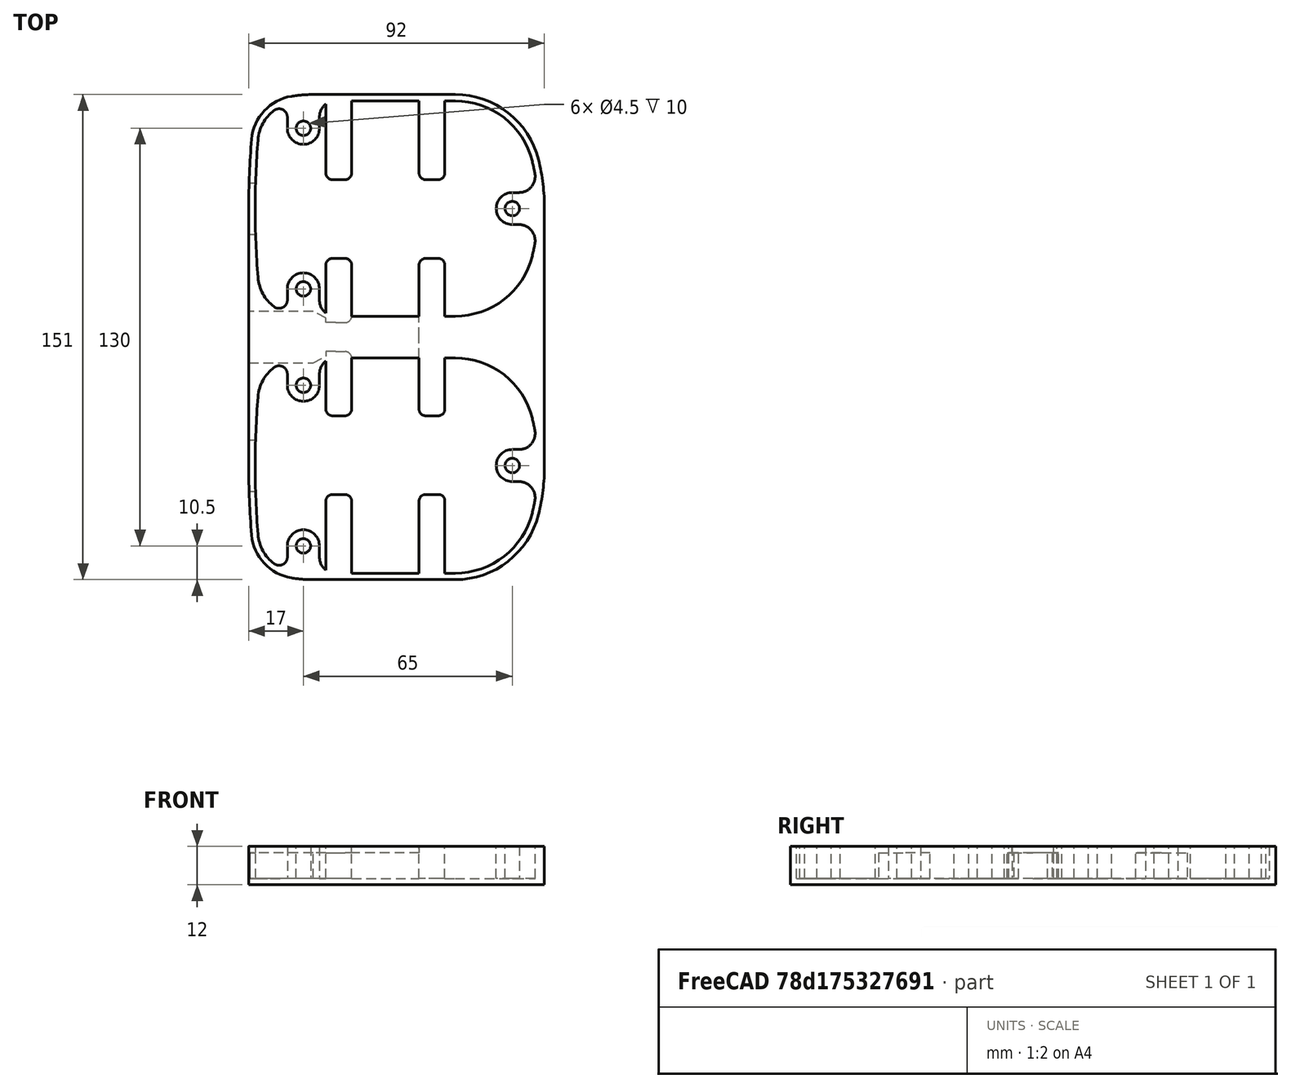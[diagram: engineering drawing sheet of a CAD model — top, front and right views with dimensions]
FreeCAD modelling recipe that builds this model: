
FCSTD DOCUMENT  (FreeCAD 0.21R33771 (Git))
Label: Makita LXT  - 18V - 2 x Bottom
License: Creative Commons Attribution 4.0
LicenseURL: https://creativecommons.org/licenses/by/4.0/
objects: Sketcher::SketchObject×6, PartDesign::Pocket×4, Mesh::Feature×3, PartDesign::Pad×2, Part::Feature×1, PartDesign::Body×1
note: 20 computed .brp shape members not serialized (recipe doc carries the construction recipe); baked Part::Feature solids carry a one-line shape summary decoded from their .brp

FEATURE [Mesh::Feature] XT60_top
  Placement = pos=(-27.47,40,-11) rot=(0,0,1;0rad)
FEATURE [Mesh::Feature] XT60_top001
  Placement = pos=(-27.47,-40,2) rot=(0,0,1;0rad)
FEATURE [Sketcher::SketchObject] Sketch
  FullyConstrained = true
  MapMode = 5
  Support = -> [XY_Plane]
  sketch-geometry (16):
    g0: ArcOfCircle CenterX=259.65 CenterY=40 CenterZ=0 NormalX=0 NormalY=0 NormalZ=1 AngleXU=0 Radius=259.65 StartAngle=3.05831 EndAngle=3.14159
    g1: ArcOfCircle CenterX=15.6319 CenterY=60.3702 CenterZ=0 NormalX=0 NormalY=0 NormalZ=1 AngleXU=0 Radius=14.7831 StartAngle=1.7292 EndAngle=3.05831
    g2: LineSegment StartX=20 StartY=75.5 StartZ=0 EndX=64.2 EndY=75.5 EndZ=0
    g3: ArcOfCircle CenterX=64.2 CenterY=48.7705 CenterZ=0 NormalX=0 NormalY=0 NormalZ=1 AngleXU=0 Radius=26.7295 StartAngle=0.24292 EndAngle=1.5708
    g4: ArcOfCircle CenterX=28.8084 CenterY=40 CenterZ=0 NormalX=0 NormalY=0 NormalZ=1 AngleXU=0 Radius=63.1916 StartAngle=0 EndAngle=0.24292
    g5: ArcOfCircle CenterX=20 CenterY=33.0247 CenterZ=0 NormalX=0 NormalY=0 NormalZ=1 AngleXU=0 Radius=42.4753 StartAngle=1.5708 EndAngle=1.7292
    g6: LineSegment StartX=0 StartY=40 StartZ=0 EndX=0 EndY=0 EndZ=0
    g7: LineSegment StartX=92 StartY=40 StartZ=0 EndX=92 EndY=0 EndZ=0
    g8: ArcOfCircle CenterX=259.65 CenterY=-40 CenterZ=0 NormalX=0 NormalY=0 NormalZ=1 AngleXU=0 Radius=259.65 StartAngle=3.14159 EndAngle=3.22488
    g9: ArcOfCircle CenterX=15.6319 CenterY=-60.3702 CenterZ=0 NormalX=0 NormalY=0 NormalZ=1 AngleXU=0 Radius=14.7831 StartAngle=3.22488 EndAngle=4.55399
    g10: LineSegment StartX=20 StartY=-75.5 StartZ=0 EndX=64.2 EndY=-75.5 EndZ=0
    g11: ArcOfCircle CenterX=64.2 CenterY=-48.7705 CenterZ=0 NormalX=0 NormalY=0 NormalZ=1 AngleXU=0 Radius=26.7295 StartAngle=4.71239 EndAngle=6.04026
    g12: ArcOfCircle CenterX=28.8084 CenterY=-40 CenterZ=0 NormalX=0 NormalY=0 NormalZ=1 AngleXU=0 Radius=63.1916 StartAngle=6.04026 EndAngle=6.28319
    g13: ArcOfCircle CenterX=20 CenterY=-33.0247 CenterZ=0 NormalX=0 NormalY=0 NormalZ=1 AngleXU=0 Radius=42.4753 StartAngle=4.55399 EndAngle=4.71239
    g14: LineSegment StartX=0 StartY=-40 StartZ=0 EndX=0 EndY=0 EndZ=0
    g15: LineSegment StartX=92 StartY=-40 StartZ=0 EndX=92 EndY=0 EndZ=0
  constraints (46):
    c: Horizontal(g2)
    c: DistanceX(g2) = 20
    c: DistanceY(g2) = 75.5
    c: DistanceX(g2,g2) = 44.2
    c: Tangent(g4,g3) = -1.5708
    c: Tangent(g3,g2) = 1.5708
    c: DistanceY(g3) = 55.2
    c: Tangent(g1,g0) = -1.5708
    c: Tangent(g5,g2) = 1.5708
    c: Tangent(g5,g1) = -1.5708
    c: DistanceX(g0) = 0.9
    c: DistanceX(g1) = 13.3
    c: DistanceY(g0) = 61.6
    c: Coincident(g6,g-1)
    c: Vertical(g6)
    c: PointOnObject(g7,g-1)
    c: Vertical(g7)
    c: Equal(g7,g6)
    c: DistanceY(g0) = 40
    c: DistanceX(g4) = 92
    c: Tangent(g7,g4) = 1.5708
    c: Tangent(g6,g0) = -1.5708
    c: Horizontal(g10)
    c: Tangent(g12,g11) = -1.5708
    c: Tangent(g11,g10) = -1.5708
    c: Tangent(g9,g8) = -1.5708
    c: Tangent(g13,g10) = -1.5708
    c: Tangent(g13,g9) = -1.5708
    c: Vertical(g14)
    c: Vertical(g15)
    c: Equal(g15,g14)
    c: Tangent(g15,g12) = -1.5708
    c: Tangent(g14,g8) = 1.5708
    c: Radius(g8) = 259.65  'Radius1'
    c: Radius(g9) = 14.7831  'Radius2'
    c: Radius(g13) = 42.4753  'Radius3'
    c: Radius(g11) = 26.7295  'Radius4'
    c: Radius(g12) = 63.1916  'Radius5'
    c: Coincident(g14,g6)
    c: Coincident(g15,g7)
    c: Equal(g12,g4)
    c: Equal(g11,g3)
    c: Equal(g5,g13)
    c: Equal(g9,g1)
    c: Symmetric(g8,g0,g-1)
    c: Symmetric(g1,g9,g-1)
FEATURE [PartDesign::Pad] Pad
  Direction = (0,0,1)
  Length = 12
  Length2 = 10
  Profile = -> Sketch
  ReferenceAxis = -> Sketch [N_Axis]
  Type = 0
FEATURE [Sketcher::SketchObject] Sketch001
  ExternalGeometry = -> [Sketch]
  FullyConstrained = false
  MapMode = 5
  Placement = pos=(0,0,12) rot=(0,0,1;0rad)
  Support = -> [Pad]
  expr: Constraints[4] = <<Sketch>>.Constraints.Radius1 - 2 mm
  expr: Constraints[5] = <<Sketch>>.Constraints.Radius4 - 2 mm
  expr: Constraints[6] = <<Sketch>>.Constraints.Radius5 - 2 mm
  sketch-geometry (68):
    g0: ArcOfCircle CenterX=15.6319 CenterY=-60.3702 CenterZ=0 NormalX=0 NormalY=0 NormalZ=1 AngleXU=0 Radius=12.7831 StartAngle=3.22488 EndAngle=4.0613
    g1: ArcOfCircle CenterX=64.2 CenterY=-48.7705 CenterZ=0 NormalX=0 NormalY=0 NormalZ=1 AngleXU=0 Radius=24.7295 StartAngle=4.71239 EndAngle=6.04026
    g2: ArcOfCircle CenterX=28.8084 CenterY=-40 CenterZ=0 NormalX=0 NormalY=0 NormalZ=1 AngleXU=0 Radius=61.1916 StartAngle=6.04026 EndAngle=6.10427
    g3: ArcOfCircle CenterX=259.65 CenterY=-40 CenterZ=0 NormalX=0 NormalY=0 NormalZ=1 AngleXU=0 Radius=257.65 StartAngle=3.14159 EndAngle=3.22488
    g4: LineSegment StartX=27 StartY=-73.5 StartZ=0 EndX=64.2 EndY=-73.5 EndZ=0
    g5: LineSegment StartX=88.2034 StartY=-54.7189 StartZ=0 EndX=90.1447 EndY=-55.2 EndZ=0
    g6: LineSegment StartX=2 StartY=-40 StartZ=0 EndX=90 EndY=-40 EndZ=0
    g7: ArcOfCircle CenterX=15.6319 CenterY=-19.6298 CenterZ=0 NormalX=0 NormalY=0 NormalZ=1 AngleXU=0 Radius=12.7831 StartAngle=2.22189 EndAngle=3.05831
    g8: ArcOfCircle CenterX=259.65 CenterY=-40 CenterZ=0 NormalX=0 NormalY=0 NormalZ=1 AngleXU=0 Radius=257.65 StartAngle=3.05831 EndAngle=3.14159
    g9: ArcOfCircle CenterX=64.2 CenterY=-31.2295 CenterZ=0 NormalX=0 NormalY=0 NormalZ=1 AngleXU=0 Radius=24.7295 StartAngle=0.24292 EndAngle=1.5708
    g10: ArcOfCircle CenterX=28.8084 CenterY=-40 CenterZ=0 NormalX=0 NormalY=0 NormalZ=1 AngleXU=0 Radius=61.1916 StartAngle=0.178916 EndAngle=0.24292
    g11: LineSegment StartX=27 StartY=-6.5 StartZ=0 EndX=64.2 EndY=-6.5 EndZ=0
    g12: Circle CenterX=17 CenterY=-15 CenterZ=0 NormalX=0 NormalY=0 NormalZ=1 AngleXU=0 Radius=2.25
    g13: Circle CenterX=17 CenterY=-65 CenterZ=0 NormalX=0 NormalY=0 NormalZ=1 AngleXU=0 Radius=2.25
    g14: Circle CenterX=82 CenterY=-40 CenterZ=0 NormalX=0 NormalY=0 NormalZ=1 AngleXU=0 Radius=2.25
    g15: ArcOfCircle CenterX=17 CenterY=-15 CenterZ=0 NormalX=0 NormalY=0 NormalZ=1 AngleXU=0 Radius=5 StartAngle=3.14159 EndAngle=6.28319
    g16: ArcOfCircle CenterX=17 CenterY=-65 CenterZ=0 NormalX=0 NormalY=0 NormalZ=1 AngleXU=0 Radius=5 StartAngle=0 EndAngle=3.14159
    g17: ArcOfCircle CenterX=82 CenterY=-40 CenterZ=0 NormalX=0 NormalY=0 NormalZ=1 AngleXU=0 Radius=5 StartAngle=1.5708 EndAngle=4.71239
    g18: LineSegment StartX=22 StartY=-15 StartZ=0 EndX=22 EndY=-11.5 EndZ=0
    g19: LineSegment StartX=12 StartY=-15 StartZ=0 EndX=12 EndY=-11.5 EndZ=0
    g20: LineSegment StartX=12 StartY=-65 StartZ=0 EndX=12 EndY=-68.5 EndZ=0
    g21: LineSegment StartX=22 StartY=-65 StartZ=0 EndX=22 EndY=-68.5 EndZ=0
    g22: LineSegment StartX=82 StartY=-45 StartZ=0 EndX=84.103 EndY=-45 EndZ=0
    g23: LineSegment StartX=82 StartY=-35 StartZ=0 EndX=84.103 EndY=-35 EndZ=0
    g24: ArcOfCircle CenterX=84.103 CenterY=-30 CenterZ=0 NormalX=0 NormalY=0 NormalZ=1 AngleXU=0 Radius=5 StartAngle=4.71239 EndAngle=6.4621
    g25: ArcOfCircle CenterX=84.103 CenterY=-50 CenterZ=0 NormalX=0 NormalY=0 NormalZ=1 AngleXU=0 Radius=5 StartAngle=6.10427 EndAngle=7.85398
    g26: ArcOfCircle CenterX=27 CenterY=-11.5 CenterZ=0 NormalX=0 NormalY=0 NormalZ=1 AngleXU=0 Radius=5 StartAngle=1.5708 EndAngle=3.14159
    g27: ArcOfCircle CenterX=9.43759 CenterY=-11.5 CenterZ=0 NormalX=0 NormalY=0 NormalZ=1 AngleXU=0 Radius=2.56241 StartAngle=0 EndAngle=2.22189
    g28: ArcOfCircle CenterX=9.43759 CenterY=-68.5 CenterZ=0 NormalX=0 NormalY=0 NormalZ=1 AngleXU=0 Radius=2.56241 StartAngle=4.0613 EndAngle=6.28319
    g29: ArcOfCircle CenterX=27 CenterY=-68.5 CenterZ=0 NormalX=0 NormalY=0 NormalZ=1 AngleXU=0 Radius=5 StartAngle=3.14159 EndAngle=4.71239
    g30: ArcOfCircle CenterX=28.8084 CenterY=-40 CenterZ=0 NormalX=0 NormalY=0 NormalZ=1 AngleXU=0 Radius=61.1916 StartAngle=6.10427 EndAngle=6.4621
    g31: LineSegment StartX=27 StartY=-6.5 StartZ=0 EndX=20 EndY=-6.5 EndZ=0
    g32: ArcOfCircle CenterX=20 CenterY=-46.9753 CenterZ=0 NormalX=0 NormalY=0 NormalZ=1 AngleXU=0 Radius=40.4753 StartAngle=1.5708 EndAngle=1.7292
    g33: ArcOfCircle CenterX=15.6319 CenterY=-19.6298 CenterZ=0 NormalX=0 NormalY=0 NormalZ=1 AngleXU=0 Radius=12.7831 StartAngle=1.7292 EndAngle=2.22189
    g34: ArcOfCircle CenterX=15.6319 CenterY=60.3702 CenterZ=0 NormalX=0 NormalY=0 NormalZ=1 AngleXU=0 Radius=12.7831 StartAngle=2.22189 EndAngle=3.05831
    g35: ArcOfCircle CenterX=64.2 CenterY=48.7705 CenterZ=0 NormalX=0 NormalY=0 NormalZ=1 AngleXU=0 Radius=24.7295 StartAngle=0.24292 EndAngle=1.5708
    g36: ArcOfCircle CenterX=28.8084 CenterY=40 CenterZ=0 NormalX=0 NormalY=0 NormalZ=1 AngleXU=0 Radius=61.1916 StartAngle=0.178916 EndAngle=0.24292
    g37: ArcOfCircle CenterX=259.65 CenterY=40 CenterZ=0 NormalX=0 NormalY=0 NormalZ=1 AngleXU=0 Radius=257.65 StartAngle=3.05831 EndAngle=3.14159
    g38: LineSegment StartX=27 StartY=73.5 StartZ=0 EndX=64.2 EndY=73.5 EndZ=0
    g39: LineSegment StartX=88.2034 StartY=54.7189 StartZ=0 EndX=90.1447 EndY=55.2 EndZ=0
    g40: LineSegment StartX=2 StartY=40 StartZ=0 EndX=90 EndY=40 EndZ=0
    g41: ArcOfCircle CenterX=15.6319 CenterY=19.6298 CenterZ=0 NormalX=0 NormalY=0 NormalZ=1 AngleXU=0 Radius=12.7831 StartAngle=3.22488 EndAngle=4.0613
    g42: ArcOfCircle CenterX=259.65 CenterY=40 CenterZ=0 NormalX=0 NormalY=0 NormalZ=1 AngleXU=0 Radius=257.65 StartAngle=3.14159 EndAngle=3.22488
    g43: ArcOfCircle CenterX=64.2 CenterY=31.2295 CenterZ=0 NormalX=0 NormalY=0 NormalZ=1 AngleXU=0 Radius=24.7295 StartAngle=4.71239 EndAngle=6.04026
    g44: ArcOfCircle CenterX=28.8084 CenterY=40 CenterZ=0 NormalX=0 NormalY=0 NormalZ=1 AngleXU=0 Radius=61.1916 StartAngle=6.04026 EndAngle=6.10427
    g45: LineSegment StartX=27 StartY=6.5 StartZ=0 EndX=64.2 EndY=6.5 EndZ=0
    g46: Circle CenterX=17 CenterY=15 CenterZ=0 NormalX=0 NormalY=0 NormalZ=1 AngleXU=0 Radius=2.25
    g47: Circle CenterX=17 CenterY=65 CenterZ=0 NormalX=0 NormalY=0 NormalZ=1 AngleXU=0 Radius=2.25
    g48: Circle CenterX=82 CenterY=40 CenterZ=0 NormalX=0 NormalY=0 NormalZ=1 AngleXU=0 Radius=2.25
    g49: ArcOfCircle CenterX=17 CenterY=15 CenterZ=0 NormalX=0 NormalY=0 NormalZ=1 AngleXU=0 Radius=5 StartAngle=4e-16 EndAngle=3.14159
    g50: ArcOfCircle CenterX=17 CenterY=65 CenterZ=0 NormalX=0 NormalY=0 NormalZ=1 AngleXU=0 Radius=5 StartAngle=3.14159 EndAngle=6.28319
    g51: ArcOfCircle CenterX=82 CenterY=40 CenterZ=0 NormalX=0 NormalY=0 NormalZ=1 AngleXU=0 Radius=5 StartAngle=1.5708 EndAngle=4.71239
    g52: LineSegment StartX=22 StartY=15 StartZ=0 EndX=22 EndY=11.5 EndZ=0
    g53: LineSegment StartX=12 StartY=15 StartZ=0 EndX=12 EndY=11.5 EndZ=0
    g54: LineSegment StartX=12 StartY=65 StartZ=0 EndX=12 EndY=68.5 EndZ=0
    g55: LineSegment StartX=22 StartY=65 StartZ=0 EndX=22 EndY=68.5 EndZ=0
    g56: LineSegment StartX=82 StartY=45 StartZ=0 EndX=84.103 EndY=45 EndZ=0
    g57: LineSegment StartX=82 StartY=35 StartZ=0 EndX=84.103 EndY=35 EndZ=0
    g58: ArcOfCircle CenterX=84.103 CenterY=30 CenterZ=0 NormalX=0 NormalY=0 NormalZ=1 AngleXU=0 Radius=5 StartAngle=6.10427 EndAngle=7.85398
    g59: ArcOfCircle CenterX=84.103 CenterY=50 CenterZ=0 NormalX=0 NormalY=0 NormalZ=1 AngleXU=0 Radius=5 StartAngle=4.71239 EndAngle=6.4621
    g60: ArcOfCircle CenterX=27 CenterY=11.5 CenterZ=0 NormalX=0 NormalY=0 NormalZ=1 AngleXU=0 Radius=5 StartAngle=3.14159 EndAngle=4.71239
    g61: ArcOfCircle CenterX=9.43759 CenterY=11.5 CenterZ=0 NormalX=0 NormalY=0 NormalZ=1 AngleXU=0 Radius=2.56241 StartAngle=4.0613 EndAngle=6.28319
    g62: ArcOfCircle CenterX=9.43759 CenterY=68.5 CenterZ=0 NormalX=0 NormalY=0 NormalZ=1 AngleXU=0 Radius=2.56241 StartAngle=0 EndAngle=2.22189
    g63: ArcOfCircle CenterX=27 CenterY=68.5 CenterZ=0 NormalX=0 NormalY=0 NormalZ=1 AngleXU=0 Radius=5 StartAngle=1.5708 EndAngle=3.14159
    g64: ArcOfCircle CenterX=28.8084 CenterY=40 CenterZ=0 NormalX=0 NormalY=0 NormalZ=1 AngleXU=0 Radius=61.1916 StartAngle=6.10427 EndAngle=6.4621
    g65: LineSegment StartX=27 StartY=6.5 StartZ=0 EndX=20 EndY=6.5 EndZ=0
    g66: ArcOfCircle CenterX=20 CenterY=46.9753 CenterZ=0 NormalX=0 NormalY=0 NormalZ=1 AngleXU=0 Radius=40.4753 StartAngle=4.55399 EndAngle=4.71239
    g67: ArcOfCircle CenterX=15.6319 CenterY=19.6298 CenterZ=0 NormalX=0 NormalY=0 NormalZ=1 AngleXU=0 Radius=12.7831 StartAngle=4.0613 EndAngle=4.55399
  constraints (164):
    c: Coincident(g0,g-4)
    c: Coincident(g2,g-8)
    c: Coincident(g2,g1)
    c: Coincident(g3,g-3)
    c: Radius(g3) = 257.65
    c: Radius(g1) = 24.7295
    c: Radius(g2) = 61.1916
    c: Coincident(g4,g1)
    c: Horizontal(g4)
    c: Vertical(g-7,g1)
    c: Horizontal(g-3,g3)
    c: Coincident(g5,g1)
    c: Coincident(g5,g-8)
    c: Perpendicular(g-8,g5)
    c: Coincident(g6,g3)
    c: Coincident(g10,g9)
    c: Coincident(g8,g7)
    c: Coincident(g11,g9)
    c: Tangent(g3,g0) = -1.5708
    c: Equal(g8,g3)
    c: Equal(g0,g7)
    c: Equal(g1,g9)
    c: Equal(g2,g10)
    c: Symmetric(g1,g9,g6)
    c: Horizontal(g11)
    c: Symmetric(g1,g9,g6)
    c: Symmetric(g7,g0,g6)
    c: Coincident(g8,g3)
    c: PointOnObject(g14,g6)
    c: Equal(g12,g13)
    c: Equal(g13,g14)
    c: Symmetric(g12,g13,g6)
    c: DistanceX(g-3,g12) = 17
    c: DistanceY(g-3,g12) = 25
    c: Diameter(g12) = 4.5
    c: DistanceX(g12,g14) = 65
    c: Coincident(g15,g12)
    c: Coincident(g16,g13)
    c: Coincident(g17,g14)
    c: Vertical(g17,g14)
    c: Vertical(g14,g17)
    c: Horizontal(g15,g12)
    c: Horizontal(g12,g15)
    c: Horizontal(g16,g13)
    c: Horizontal(g13,g16)
    c: Equal(g16,g15)
    c: Equal(g15,g17)
    c: Diameter(g15) = 10
    c: Coincident(g18,g15)
    c: Vertical(g18)
    c: Coincident(g19,g15)
    c: Coincident(g20,g16)
    c: Vertical(g20)
    c: Coincident(g21,g16)
    c: Vertical(g21)
    c: Coincident(g22,g17)
    c: Coincident(g23,g17)
    c: Equal(g23,g22)
    c: Equal(g21,g18)
    c: Equal(g19,g20)
    c: Horizontal(g22)
    c: Coincident(g26,g18)
    c: Equal(g29,g26)
    c: Equal(g28,g27)
    c: Tangent(g27,g19) = -1.5708
    c: Equal(g18,g19)
    c: Tangent(g29,g21) = -1.5708
    c: Tangent(g28,g20) = 1.5708
    c: Equal(g26,g15)
    c: Tangent(g24,g23) = -1.5708
    c: Tangent(g25,g22) = 1.5708
    c: Equal(g24,g17)
    c: Tangent(g10,g24) = -1.5708
    c: Tangent(g2,g25) = -1.5708
    c: Coincident(g30,g2)
    c: Coincident(g30,g10)
    c: Coincident(g30,g2)
    c: Symmetric(g10,g2,g6)
    c: PointOnObject(g6,g30)
    c: Tangent(g11,g26) = 1.5708
    c: Tangent(g7,g27) = -1.5708
    c: Coincident(g31,g11)
    c: Equal(g33,g7)
    c: Tangent(g33,g32) = -1.5708
    c: Tangent(g4,g29) = -1.5708
    c: Tangent(g0,g28) = -1.5708
    c: DistanceY(g-7,g1) = 2
    c: Vertical(g19)
    c: Tangent(g33,g7) = -1.5708
    c: Tangent(g32,g31) = -1.5708
    c: Symmetric(g32,g-5,g6)
    c: Coincident(g36,g35)
    c: Radius(g37) = 257.65
    c: Radius(g35) = 24.7295
    c: Radius(g36) = 61.1916
    c: Coincident(g38,g35)
    c: Horizontal(g38)
    c: Coincident(g39,g35)
    c: Coincident(g40,g37)
    c: Coincident(g44,g43)
    c: Coincident(g42,g41)
    c: Coincident(g45,g43)
    c: Tangent(g37,g34) = -1.5708
    c: Equal(g42,g37)
    c: Equal(g34,g41)
    c: Equal(g35,g43)
    c: Equal(g36,g44)
    c: Symmetric(g35,g43,g40)
    c: Horizontal(g45)
    c: Symmetric(g35,g43,g40)
    c: Symmetric(g41,g34,g40)
    c: Coincident(g42,g37)
    c: PointOnObject(g48,g40)
    c: Equal(g46,g47)
    c: Equal(g47,g48)
    c: Symmetric(g46,g47,g40)
    c: Diameter(g46) = 4.5
    c: Coincident(g49,g46)
    c: Coincident(g50,g47)
    c: Coincident(g51,g48)
    c: Equal(g50,g49)
    c: Equal(g49,g51)
    c: Diameter(g49) = 10
    c: Coincident(g52,g49)
    c: Vertical(g52)
    c: Coincident(g53,g49)
    c: Coincident(g54,g50)
    c: Vertical(g54)
    c: Coincident(g55,g50)
    c: Vertical(g55)
    c: Coincident(g56,g51)
    c: Coincident(g57,g51)
    c: Equal(g57,g56)
    c: Equal(g55,g52)
    c: Equal(g53,g54)
    c: Horizontal(g56)
    c: Coincident(g60,g52)
    c: Equal(g63,g60)
    c: Equal(g62,g61)
    c: Tangent(g61,g53) = 1.5708
    c: Equal(g52,g53)
    c: Tangent(g63,g55) = 1.5708
    c: Tangent(g62,g54) = -1.5708
    c: Equal(g60,g49)
    c: Tangent(g58,g57) = 1.5708
    c: Tangent(g59,g56) = -1.5708
    c: Equal(g58,g51)
    c: Tangent(g44,g58) = -1.5708
    c: Tangent(g36,g59) = -1.5708
    c: Coincident(g64,g36)
    c: Coincident(g64,g44)
    c: Coincident(g64,g36)
    c: Symmetric(g44,g36,g40)
    c: PointOnObject(g40,g64)
    c: Tangent(g45,g60) = -1.5708
    c: Tangent(g41,g61) = -1.5708
    c: Coincident(g65,g45)
    c: Equal(g67,g41)
    c: Tangent(g67,g66) = -1.5708
    c: Tangent(g38,g63) = 1.5708
    c: Tangent(g34,g62) = -1.5708
    c: Vertical(g53)
    c: Tangent(g67,g41) = -1.5708
    c: Tangent(g66,g65) = 1.5708
FEATURE [PartDesign::Pocket] Pocket
  BaseFeature = -> Pad
  Direction = (0,0,-1)
  Length = 10
  Length2 = 5
  Profile = -> Sketch001
  ReferenceAxis = -> Sketch001 [N_Axis]
  Type = 0
FEATURE [Mesh::Feature] makita_t_mount_M3
  Placement = pos=(-27.47,-40,0) rot=(0,0,1;0rad)
FEATURE [Sketcher::SketchObject] Sketch002
  FullyConstrained = false
  MapMode = 5
  Placement = pos=(0,0,0) rot=(0.57735,0.57735,0.57735;2.0944rad)
  Support = -> [YZ_Plane]
  sketch-geometry (10):
    g0: LineSegment StartX=-48 StartY=10 StartZ=0 EndX=-48 EndY=2 EndZ=0
    g1: LineSegment StartX=-48 StartY=2 StartZ=0 EndX=-32 EndY=2 EndZ=0
    g2: LineSegment StartX=-32 StartY=2 StartZ=0 EndX=-32 EndY=10 EndZ=0
    g3: LineSegment StartX=-32 StartY=10 StartZ=0 EndX=-48 EndY=10 EndZ=0
    g4: GeomPoint X=-40 Y=6 Z=0
    g5: LineSegment StartX=48 StartY=10 StartZ=0 EndX=48 EndY=2 EndZ=0
    g6: LineSegment StartX=48 StartY=2 StartZ=0 EndX=32 EndY=2 EndZ=0
    g7: LineSegment StartX=32 StartY=2 StartZ=0 EndX=32 EndY=10 EndZ=0
    g8: LineSegment StartX=32 StartY=10 StartZ=0 EndX=48 EndY=10 EndZ=0
    g9: GeomPoint X=40 Y=6 Z=0
  constraints (22):
    c: Coincident(g0,g1)
    c: Coincident(g1,g2)
    c: Coincident(g2,g3)
    c: Coincident(g3,g0)
    c: Horizontal(g1)
    c: Horizontal(g3)
    c: Vertical(g0)
    c: Vertical(g2)
    c: Symmetric(g1,g0,g4)
    c: DistanceX(g3,g3) = 16
    c: DistanceY(g0,g0) = 8
    c: DistanceY(g-1,g4) = 6
    c: DistanceX(g4,g-1) = 40
    c: Coincident(g5,g6)
    c: Coincident(g6,g7)
    c: Coincident(g7,g8)
    c: Coincident(g8,g5)
    c: Horizontal(g6)
    c: Horizontal(g8)
    c: Vertical(g5)
    c: Vertical(g7)
    c: Symmetric(g6,g5,g9)
FEATURE [PartDesign::Pocket] Pocket001
  BaseFeature = -> Pocket
  Direction = (-1,2e-16,-3e-16)
  Length = 10
  Length2 = 5
  Profile = -> Sketch002
  ReferenceAxis = -> Sketch002 [N_Axis]
  Reversed = true
  Type = 0
FEATURE [Sketcher::SketchObject] Sketch003
  FullyConstrained = true
  MapMode = 5
  Placement = pos=(0,0,0) rot=(1,0,0;1.5708rad)
  Support = -> [XZ_Plane]
  sketch-geometry (5):
    g0: LineSegment StartX=27 StartY=10 StartZ=0 EndX=27 EndY=2 EndZ=0
    g1: LineSegment StartX=27 StartY=2 StartZ=0 EndX=57 EndY=2 EndZ=0
    g2: LineSegment StartX=57 StartY=2 StartZ=0 EndX=57 EndY=10 EndZ=0
    g3: LineSegment StartX=57 StartY=10 StartZ=0 EndX=27 EndY=10 EndZ=0
    g4: GeomPoint X=42 Y=6 Z=0
  constraints (13):
    c: Coincident(g0,g1)
    c: Coincident(g1,g2)
    c: Coincident(g2,g3)
    c: Coincident(g3,g0)
    c: Horizontal(g1)
    c: Horizontal(g3)
    c: Vertical(g0)
    c: Vertical(g2)
    c: Symmetric(g1,g0,g4)
    c: DistanceY(g2,g2) = 8
    c: DistanceX(g3,g3) = 30
    c: DistanceX(g4) = 42
    c: DistanceY(g4) = 6
FEATURE [PartDesign::Pocket] Pocket002
  BaseFeature = -> Pocket001
  Direction = (0,1,2e-16)
  Length = 13
  Length2 = 5
  Midplane = true
  Profile = -> Sketch003
  ReferenceAxis = -> Sketch003 [N_Axis]
  Type = 0
FEATURE [Part::Feature] makita_t_mount_M004
  Placement = pos=(0,0,15) rot=(0,0,1;0rad)
  shape: bbox 92.05 x 71 x 21.06 mm, 5616 faces, 0 solids (baked)
FEATURE [PartDesign::Body] Body  label="Makita 18V x 2 base"
  Group = -> [Sketch,Pad,Sketch001,Pocket,Sketch002,Pocket001,Sketch003,Pocket002,Sketch007,Pocket003,Sketch008,Pad001]
  Origin = -> Origin
  Tip = -> Pad001
FEATURE [Sketcher::SketchObject] Sketch007
  FullyConstrained = false
  MapMode = 5
  Placement = pos=(0,0,2) rot=(0,0,1;0rad)
  Support = -> [Pocket003]
  sketch-geometry (6):
    g0: LineSegment StartX=0 StartY=8 StartZ=0 EndX=0 EndY=-8 EndZ=0
    g1: LineSegment StartX=0 StartY=-8 StartZ=0 EndX=20 EndY=-8 EndZ=0
    g2: LineSegment StartX=20 StartY=8 StartZ=0 EndX=0 EndY=8 EndZ=0
    g3: LineSegment StartX=27 StartY=4.5 StartZ=0 EndX=27 EndY=-4.5 EndZ=0
    g4: LineSegment StartX=27 StartY=4.5 StartZ=0 EndX=20 EndY=8 EndZ=0
    g5: LineSegment StartX=20 StartY=-8 StartZ=0 EndX=27 EndY=-4.5 EndZ=0
  constraints (16):
    c: PointOnObject(g0,g-2)
    c: Coincident(g0,g1)
    c: Horizontal(g1)
    c: Coincident(g2,g0)
    c: Horizontal(g2)
    c: Symmetric(g0,g0,g-1)
    c: Equal(g2,g1)
    c: DistanceY(g0,g0) = 16
    c: DistanceX(g2,g2) = 20
    c: DistanceY(g3,g3) = 9
    c: Vertical(g3)
    c: Coincident(g4,g3)
    c: Coincident(g5,g1)
    c: Coincident(g5,g3)
    c: Equal(g4,g5)
    c: Coincident(g4,g2)
FEATURE [PartDesign::Pocket] Pocket003
  BaseFeature = -> Pocket002
  Direction = (0,0,-1)
  Length = 8
  Length2 = 5
  Profile = -> Sketch007
  ReferenceAxis = -> Sketch007 [N_Axis]
  Reversed = true
  Type = 0
FEATURE [Sketcher::SketchObject] Sketch008
  ExternalGeometry = -> [Pocket003]
  FullyConstrained = false
  MapMode = 5
  Placement = pos=(0,0,2) rot=(0,0,1;0rad)
  Support = -> [Pocket003]
  sketch-geometry (48):
    g0: LineSegment StartX=24 StartY=-4.5 StartZ=0 EndX=24 EndY=-22.5 EndZ=0
    g1: LineSegment StartX=26 StartY=-24.5 StartZ=0 EndX=30 EndY=-24.5 EndZ=0
    g2: LineSegment StartX=32 StartY=-22.5 StartZ=0 EndX=32 EndY=-6.5 EndZ=0
    g3: LineSegment StartX=30 StartY=-4.5 StartZ=0 EndX=24 EndY=-4.5 EndZ=0
    g4: LineSegment StartX=53 StartY=0 StartZ=0 EndX=53 EndY=-22.5 EndZ=0
    g5: LineSegment StartX=55 StartY=-24.5 StartZ=0 EndX=59 EndY=-24.5 EndZ=0
    g6: LineSegment StartX=61 StartY=-22.5 StartZ=0 EndX=61 EndY=0 EndZ=0
    g7: LineSegment StartX=24 StartY=-51 StartZ=0 EndX=24 EndY=-73.5 EndZ=0
    g8: LineSegment StartX=24 StartY=-73.5 StartZ=0 EndX=32 EndY=-73.5 EndZ=0
    g9: LineSegment StartX=32 StartY=-73.5 StartZ=0 EndX=32 EndY=-51 EndZ=0
    g10: LineSegment StartX=30 StartY=-49 StartZ=0 EndX=26 EndY=-49 EndZ=0
    g11: LineSegment StartX=53 StartY=-51 StartZ=0 EndX=53 EndY=-73.5 EndZ=0
    g12: LineSegment StartX=53 StartY=-73.5 StartZ=0 EndX=61 EndY=-73.5 EndZ=0
    g13: LineSegment StartX=61 StartY=-73.5 StartZ=0 EndX=61 EndY=-51 EndZ=0
    g14: LineSegment StartX=59 StartY=-49 StartZ=0 EndX=55 EndY=-49 EndZ=0
    g15: ArcOfCircle CenterX=59 CenterY=-22.5 CenterZ=0 NormalX=0 NormalY=0 NormalZ=1 AngleXU=0 Radius=2 StartAngle=4.71239 EndAngle=6.28319
    g16: ArcOfCircle CenterX=55 CenterY=-22.5 CenterZ=0 NormalX=0 NormalY=0 NormalZ=1 AngleXU=0 Radius=2 StartAngle=3.14159 EndAngle=4.71239
    g17: ArcOfCircle CenterX=30 CenterY=-22.5 CenterZ=0 NormalX=0 NormalY=0 NormalZ=1 AngleXU=0 Radius=2 StartAngle=4.71239 EndAngle=6.28319
    g18: ArcOfCircle CenterX=26 CenterY=-22.5 CenterZ=0 NormalX=0 NormalY=0 NormalZ=1 AngleXU=0 Radius=2 StartAngle=3.14159 EndAngle=4.71239
    g19: ArcOfCircle CenterX=26 CenterY=-51 CenterZ=0 NormalX=0 NormalY=0 NormalZ=1 AngleXU=0 Radius=2 StartAngle=1.5708 EndAngle=3.14159
    g20: ArcOfCircle CenterX=30 CenterY=-51 CenterZ=0 NormalX=0 NormalY=0 NormalZ=1 AngleXU=0 Radius=2 StartAngle=0 EndAngle=1.5708
    g21: ArcOfCircle CenterX=55 CenterY=-51 CenterZ=0 NormalX=0 NormalY=0 NormalZ=1 AngleXU=0 Radius=2 StartAngle=1.5708 EndAngle=3.14159
    g22: ArcOfCircle CenterX=59 CenterY=-51 CenterZ=0 NormalX=0 NormalY=0 NormalZ=1 AngleXU=0 Radius=2 StartAngle=-9e-16 EndAngle=1.5708
    g23: ArcOfCircle CenterX=30 CenterY=-6.5 CenterZ=0 NormalX=0 NormalY=0 NormalZ=1 AngleXU=0 Radius=2 StartAngle=0 EndAngle=1.5708
    g24: LineSegment StartX=24 StartY=4.5 StartZ=0 EndX=24 EndY=22.5 EndZ=0
    g25: LineSegment StartX=26 StartY=24.5 StartZ=0 EndX=30 EndY=24.5 EndZ=0
    g26: LineSegment StartX=32 StartY=22.5 StartZ=0 EndX=32 EndY=6.5 EndZ=0
    g27: LineSegment StartX=30 StartY=4.5 StartZ=0 EndX=24 EndY=4.5 EndZ=0
    g28: LineSegment StartX=53 StartY=0 StartZ=0 EndX=53 EndY=22.5 EndZ=0
    g29: LineSegment StartX=55 StartY=24.5 StartZ=0 EndX=59 EndY=24.5 EndZ=0
    g30: LineSegment StartX=61 StartY=22.5 StartZ=0 EndX=61 EndY=0 EndZ=0
    g31: LineSegment StartX=24 StartY=51 StartZ=0 EndX=24 EndY=73.5 EndZ=0
    g32: LineSegment StartX=24 StartY=73.5 StartZ=0 EndX=32 EndY=73.5 EndZ=0
    g33: LineSegment StartX=32 StartY=73.5 StartZ=0 EndX=32 EndY=51 EndZ=0
    g34: LineSegment StartX=30 StartY=49 StartZ=0 EndX=26 EndY=49 EndZ=0
    g35: LineSegment StartX=53 StartY=51 StartZ=0 EndX=53 EndY=73.5 EndZ=0
    g36: LineSegment StartX=53 StartY=73.5 StartZ=0 EndX=61 EndY=73.5 EndZ=0
    g37: LineSegment StartX=61 StartY=73.5 StartZ=0 EndX=61 EndY=51 EndZ=0
    g38: LineSegment StartX=59 StartY=49 StartZ=0 EndX=55 EndY=49 EndZ=0
    g39: ArcOfCircle CenterX=59 CenterY=22.5 CenterZ=0 NormalX=0 NormalY=0 NormalZ=1 AngleXU=0 Radius=2 StartAngle=0 EndAngle=1.5708
    g40: ArcOfCircle CenterX=55 CenterY=22.5 CenterZ=0 NormalX=0 NormalY=0 NormalZ=1 AngleXU=0 Radius=2 StartAngle=1.5708 EndAngle=3.14159
    g41: ArcOfCircle CenterX=30 CenterY=22.5 CenterZ=0 NormalX=0 NormalY=0 NormalZ=1 AngleXU=0 Radius=2 StartAngle=0 EndAngle=1.5708
    g42: ArcOfCircle CenterX=26 CenterY=22.5 CenterZ=0 NormalX=0 NormalY=0 NormalZ=1 AngleXU=0 Radius=2 StartAngle=1.5708 EndAngle=3.14159
    g43: ArcOfCircle CenterX=26 CenterY=51 CenterZ=0 NormalX=0 NormalY=0 NormalZ=1 AngleXU=0 Radius=2 StartAngle=3.14159 EndAngle=4.71239
    g44: ArcOfCircle CenterX=30 CenterY=51 CenterZ=0 NormalX=0 NormalY=0 NormalZ=1 AngleXU=0 Radius=2 StartAngle=4.71239 EndAngle=6.28319
    g45: ArcOfCircle CenterX=55 CenterY=51 CenterZ=0 NormalX=0 NormalY=0 NormalZ=1 AngleXU=0 Radius=2 StartAngle=3.14159 EndAngle=4.71239
    g46: ArcOfCircle CenterX=59 CenterY=51 CenterZ=0 NormalX=0 NormalY=0 NormalZ=1 AngleXU=0 Radius=2 StartAngle=4.71239 EndAngle=6.28319
    g47: ArcOfCircle CenterX=30 CenterY=6.5 CenterZ=0 NormalX=0 NormalY=0 NormalZ=1 AngleXU=0 Radius=2 StartAngle=4.71239 EndAngle=6.28319
  constraints (116):
    c: Coincident(g3,g0)
    c: Horizontal(g1)
    c: Horizontal(g3)
    c: Vertical(g0)
    c: Vertical(g2)
    c: Horizontal(g5)
    c: Vertical(g4)
    c: Vertical(g6)
    c: Coincident(g7,g8)
    c: Coincident(g8,g9)
    c: Horizontal(g8)
    c: Horizontal(g10)
    c: Vertical(g7)
    c: Vertical(g9)
    c: Coincident(g11,g12)
    c: Coincident(g12,g13)
    c: Horizontal(g12)
    c: Horizontal(g14)
    c: Vertical(g11)
    c: Vertical(g13)
    c: Tangent(g5,g15) = -1.5708
    c: Tangent(g6,g15) = -1.5708
    c: Tangent(g4,g16) = -1.5708
    c: Tangent(g5,g16) = -1.5708
    c: Tangent(g2,g17) = -1.5708
    c: Tangent(g1,g17) = -1.5708
    c: Tangent(g0,g18) = -1.5708
    c: Tangent(g1,g18) = -1.5708
    c: Tangent(g7,g19) = -1.5708
    c: Tangent(g10,g19) = -1.5708
    c: Tangent(g9,g20) = -1.5708
    c: Tangent(g10,g20) = -1.5708
    c: Tangent(g11,g21) = -1.5708
    c: Tangent(g14,g21) = -1.5708
    c: Tangent(g13,g22) = -1.5708
    c: Tangent(g14,g22) = -1.5708
    c: Equal(g4,g11)
    c: Equal(g11,g9)
    c: Tangent(g2,g23) = -1.5708
    c: Tangent(g3,g23) = -1.5708
    c: Equal(g19,g20)
    c: Equal(g20,g18)
    c: Equal(g18,g17)
    c: Equal(g17,g16)
    c: Equal(g16,g15)
    c: PointOnObject(g4,g-1)
    c: Equal(g1,g10)
    c: Equal(g10,g14)
    c: Equal(g14,g5)
    c: Radius(g17) = 2
    c: Equal(g15,g21)
    c: Equal(g21,g22)
    c: Vertical(g11,g4)
    c: Vertical(g7,g0)
    c: Horizontal(g0,g-3)
    c: DistanceX(g0) = 24
    c: DistanceY(g1,g-1) = 24.5
    c: Horizontal(g1,g5)
    c: DistanceX(g1,g1) = 4
    c: DistanceX(g4) = 53
    c: Equal(g18,g23)
    c: PointOnObject(g8,g-4)
    c: PointOnObject(g11,g-4)
    c: PointOnObject(g6,g-1)
    c: Coincident(g27,g24)
    c: Horizontal(g25)
    c: Horizontal(g27)
    c: Vertical(g24)
    c: Vertical(g26)
    c: Horizontal(g29)
    c: Vertical(g28)
    c: Vertical(g30)
    c: Coincident(g31,g32)
    c: Coincident(g32,g33)
    c: Horizontal(g32)
    c: Horizontal(g34)
    c: Vertical(g31)
    c: Vertical(g33)
    c: Coincident(g35,g36)
    c: Coincident(g36,g37)
    c: Horizontal(g36)
    c: Horizontal(g38)
    c: Vertical(g35)
    c: Vertical(g37)
    c: Tangent(g29,g39) = 1.5708
    c: Tangent(g30,g39) = 1.5708
    c: Tangent(g28,g40) = 1.5708
    c: Tangent(g29,g40) = 1.5708
    c: Tangent(g26,g41) = 1.5708
    c: Tangent(g25,g41) = 1.5708
    c: Tangent(g24,g42) = 1.5708
    c: Tangent(g25,g42) = 1.5708
    c: Tangent(g31,g43) = 1.5708
    c: Tangent(g34,g43) = 1.5708
    c: Tangent(g33,g44) = 1.5708
    c: Tangent(g34,g44) = 1.5708
    c: Tangent(g35,g45) = 1.5708
    c: Tangent(g38,g45) = 1.5708
    c: Tangent(g37,g46) = 1.5708
    c: Tangent(g38,g46) = 1.5708
    c: Equal(g28,g35)
    c: Equal(g35,g33)
    c: Tangent(g26,g47) = 1.5708
    c: Tangent(g27,g47) = 1.5708
    c: Equal(g43,g44)
    c: Equal(g44,g42)
    c: Equal(g42,g41)
    c: Equal(g41,g40)
    c: Equal(g40,g39)
    c: Equal(g25,g34)
    c: Equal(g34,g38)
    c: Equal(g38,g29)
    c: Radius(g41) = 2
    c: Equal(g39,g45)
    c: Equal(g45,g46)
    c: Equal(g42,g47)
FEATURE [PartDesign::Pad] Pad001
  BaseFeature = -> Pocket003
  Direction = (0,0,1)
  Length = 10
  Length2 = 10
  Profile = -> Sketch008
  ReferenceAxis = -> Sketch008 [N_Axis]
  Type = 0
